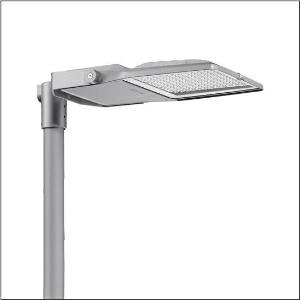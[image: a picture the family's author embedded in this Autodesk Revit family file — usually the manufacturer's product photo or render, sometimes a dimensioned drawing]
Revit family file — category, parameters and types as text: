
# Revit family: floodlight_fl_21_iq_midi___pl33t_5xa7781e2f3a_de32
name_source: partatom
category: Lighting Fixtures
units: mm (PartAtom-declared; Revit-internal decimal feet)

## family parameters
Cut with Voids When Loaded = No
Host = Face
Light Source = No
Part Type = Normal
Room Calculation Point = No
Round Connector Dimension = Use Diameter
Shared = No

## types (1)
- --- (1 x LED, 26540 lm, 208.1 W, 3000K)
    Apparent Load = 208 VA
    CIE Flux Codes = 26 75 99 100 100
    Color Rendering = 70
    Color Temperature = 3000K
    Default Elevation = 1800 mm
    Description = Floodlight FL 21 iQ midi, floodlight, primary light control with lens, of PMMA, primary optical cover: protective disc, of toughened safety glass, transparent, light distribution: PL33T, light emission: direct distribution, installation type: surface-mounted, LED, High Power LED, rated luminous flux: 26.540lm, luminous efficacy: 128lm/W, light colour: 730, colour temperature: 3000K, control gear: ECG iQ, control: optimised constant luminous flux control (CLO 2.0), Desk-Remote (wireless, voltage-free reading and setting of iQ features in the workshop via application-optimized NFC function/RFID function), Light-Fading, Smart-Wire, Night-Set, Lumen-Switch, Temp-Guard, Auto-Match, with terminal, 6-pole, mains connection: 220..240V, AC, 50/60Hz, start of lifetime: 208W, end of service life: 227W, reduction: 90W, luminaire housing, of diecast aluminium, powder-coated, Siteco® metallic grey (DB 702S), corrosivity category C5 mid according to DIN EN ISO 12944, sealing non-destructively replaceable, please order mast flange separately, mast bracket, of steel, galvanised, powder-coated, Siteco® metallic grey (DB 702S), protection rating (complete): IP66, insulation class (complete): insulation class II (safety insulation), certification: CE, protection symbol: D, impact resistance: IK08, permissible operating ambient temperature: -40..+40°C, permissible operating ambient temperature for outdoor applications: -40..+50°C, standard: DIN EN 12944, LABS conformity tested according to VDMA 24364:2018-05, packaging unit: 1 piece

Light Distribution: PL33T
    Height = 76 mm
    Lamp = 1 x LED
    Lamp Light Flux = 26540 lm
    Lamp Power = 208.1 W
    Lamp count = 1
    Length = 657 mm
    Luminous efficacy = 128 lm/W
    Manufacturer = Siteco
    ModVariant = No
    Model = 5XA7781E2F3A
    Number of Poles = 1
    OnlyDefault = Yes
    Power Factor = 1
    Product Name = Floodlight FL 21 iQ midi | PL33T
    Product group = floodlight | pylon annexe
    ProductGroupID = 6200
    Protection Class = Protection class II
    Protection Degree = IP 66
    RLX_Detail_Level = 1
    RLX_Emergency_Light_Flux = 0 lm
    RLX_Emergency_Type = 0
    RLX_Emergency_Type_DB = No
    RlxData = <blob elided: 153613 chars, md5=4f1c7444>
    Socket = socket
    Standby Power = 0 W
    System Light Flux = 26540 lm
    System Power = 208 W
    Type Comments = factory setting: luminous flux: 100 % | dim-lin: 254 | 710 mA
    Type Image = l_1007123.jpg
    URL = http://relux.com
    VarID = @adj_052305
    Voltage = 0 V
    Weight = 0.00 kg
    Width = 442 mm

## geometry (parser evidence)
native form markers: Blend x4, Sweep x12
no freeform markers — native parametric forms only
